# Revit family: Grate-Floor_Drain-Whitehall-BestCare-WHDG-SQ-SS_Series
name_source: partatom
category: Plumbing Fixtures
units: mm (PartAtom-declared; Revit-internal decimal feet)

## family parameters
Always vertical = No
Cut with Voids When Loaded = No
OmniClass Number = 23.70.50.21.24
OmniClass Title = Waste Water Drains
Part Type = Normal
Room Calculation Point = No
Round Connector Dimension = Use Diameter
Shared = Yes
Work Plane-Based = Yes

## types (2) — shared parameters
Assembly Code = D2030300
CW Connection = No
Default Elevation = 0"
Description = BestCare® Ligature-Resistant Floor Drain Grate - Stainless Steel
Finish = Metal-Whitehall-Stainless Steel
HW Connection = No
Height = 7/8"
Installation Type = Floor Mounted
Manufacturer = Whitehall Mfg.
Material = Metal-Whitehall-Stainless Steel
Product Documentation Link = https://www.whitehallmfg.com
Product Page URL = https://www.whitehallmfg.com
Type Comments = Appropriate for Poured Finished Floors.For use in JR SMITH Floor Drains.
URL = https://www.whitehallmfg.com
Vent Connection = No
Waste Connection = No

## per-type parameters (varying)
| type | Keynote | Length | Width |
| WHDG-5SQ-SS | 5” Square Stn Stl Floor Drain Grate Only | 5" | 5" |
| WHDG-6SQ-SS | 6” Square Stn Stl Floor Drain Grate Only | 6" | 6" |

note: column(s) folded — value = type name in every type: Model

## geometry (parser evidence)
native form markers: Sweep x2
no freeform markers — native parametric forms only
